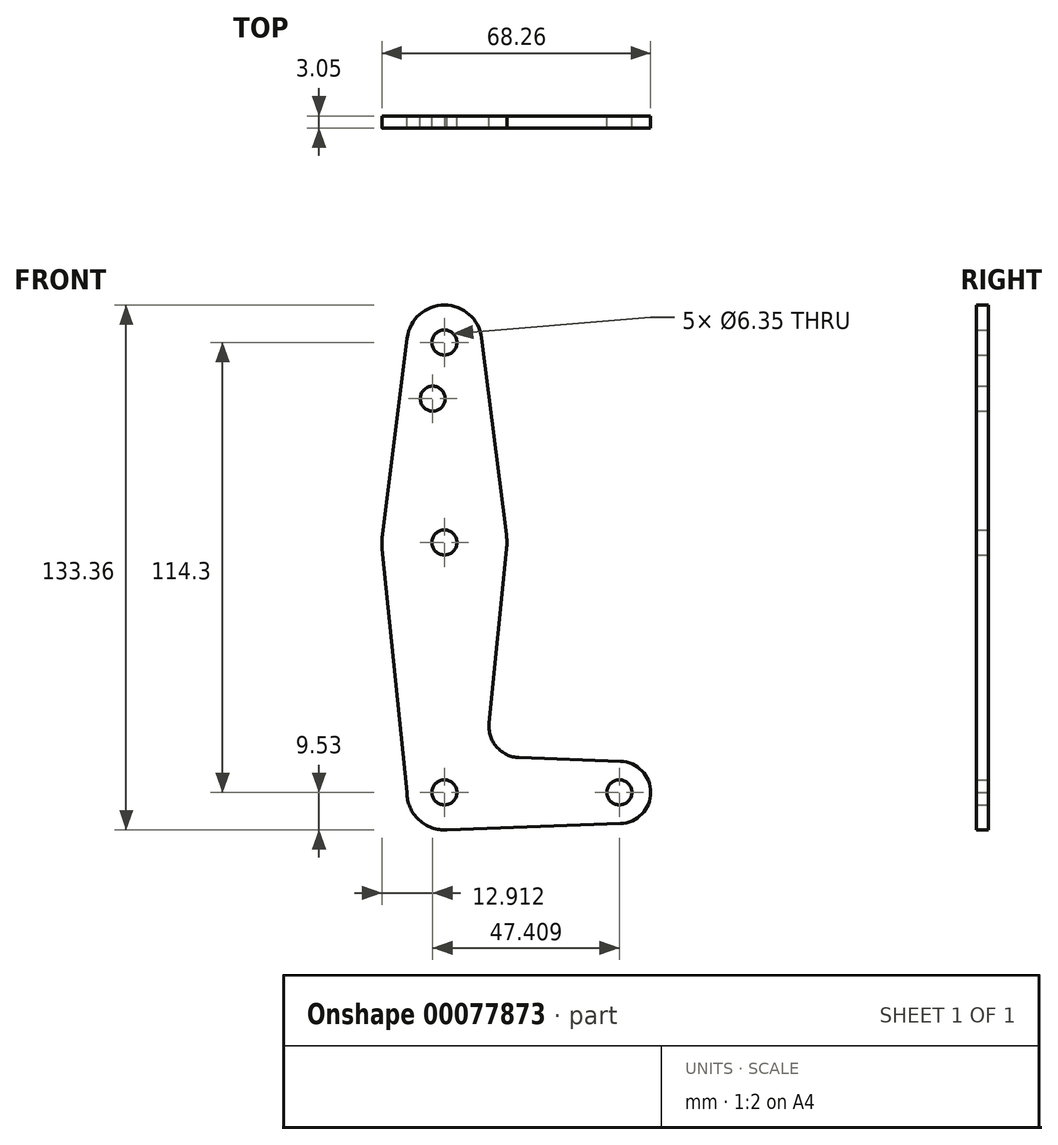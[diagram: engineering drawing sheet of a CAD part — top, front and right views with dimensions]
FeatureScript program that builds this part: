
annotation { "Feature Type Name" : "Feature", "Feature Type Description" : "" }
export const myFeature = defineFeature(function(context is Context, id is Id, definition is map)
    precondition{}
    {
        {
            var Q0;
            Q0=qCreatedBy(makeId("Front.planeOp"),FACE);
            cPlane(context, id + "F0", {"entities" : qUnion([Q0]), "cplaneType" : CPlaneType.OFFSET, "offset" : 152.4 * mm, "width" : 152.4 * mm, "height" : 152.4 * mm});
        }
        {
            var Q0;
            Q0=qCreatedBy(id+"F0.planeOp",FACE);
            var sketch = newSketch(context, id + "F1", { "sketchPlane" : qUnion([Q0])});
            skLineSegment(sketch, "E0", {"start": v(0, 0) * mm, "end": v(0, 114.3) * mm, "construction": true});
            skLineSegment(sketch, "E1", {"start": v(0, 0) * mm, "end": v(44.45, 0) * mm, "construction": true});
            skCircle(sketch, "E2", {"center": v(0, 114.3) * mm, "radius": 9.53 * mm});
            skCircle(sketch, "E3", {"center": v(0, 63.5) * mm, "radius": 15.88 * mm});
            skCircle(sketch, "E4", {"center": v(0, 0) * mm, "radius": 9.53 * mm});
            skCircle(sketch, "E5", {"center": v(44.45, 0) * mm, "radius": 7.94 * mm});
            skLineSegment(sketch, "E6", {"start": v(-9.45, 115.5) * mm, "end": v(-15.75, 65.48) * mm});
            skLineSegment(sketch, "E7", {"start": v(9.45, 115.5) * mm, "end": v(15.75, 65.48) * mm});
            skLineSegment(sketch, "E8", {"start": v(18.97, 8.85) * mm, "end": v(44.73, 7.93) * mm});
            skLineSegment(sketch, "E9", {"start": v(0, -9.53) * mm, "end": v(44.73, -7.93) * mm});
            skLineSegment(sketch, "E10", {"start": v(-9.53, 0) * mm, "end": v(-15.8, 61.9) * mm});
            skLineSegment(sketch, "E11", {"start": v(15.8, 61.9) * mm, "end": v(11.34, 17.59) * mm});
            skCircle(sketch, "E12", {"center": v(0, 63.5) * mm, "radius": 3.18 * mm});
            skCircle(sketch, "E13", {"center": v(0, 114.3) * mm, "radius": 3.18 * mm});
            skCircle(sketch, "E14", {"center": v(0, 0) * mm, "radius": 3.18 * mm});
            skCircle(sketch, "E15", {"center": v(44.45, 0) * mm, "radius": 3.18 * mm});
            skCircle(sketch, "E16", {"center": v(-2.96, 100.03) * mm, "radius": 3.18 * mm});
            skArc(sketch, "E17.filletArc", {"start": v(11.34, 17.59) * mm, "mid": v(13.26, 11.57) * mm, "end": v(18.97, 8.85) * mm});
            skSolve(sketch);
        }
        {
            var Q0;
            Q0 = qSketchRegion(id + "F1", true);
            extrude(context, id + "F2", {"entities" : qUnion([Q0]), "depth" : 3.05 * mm});
        }
    });
